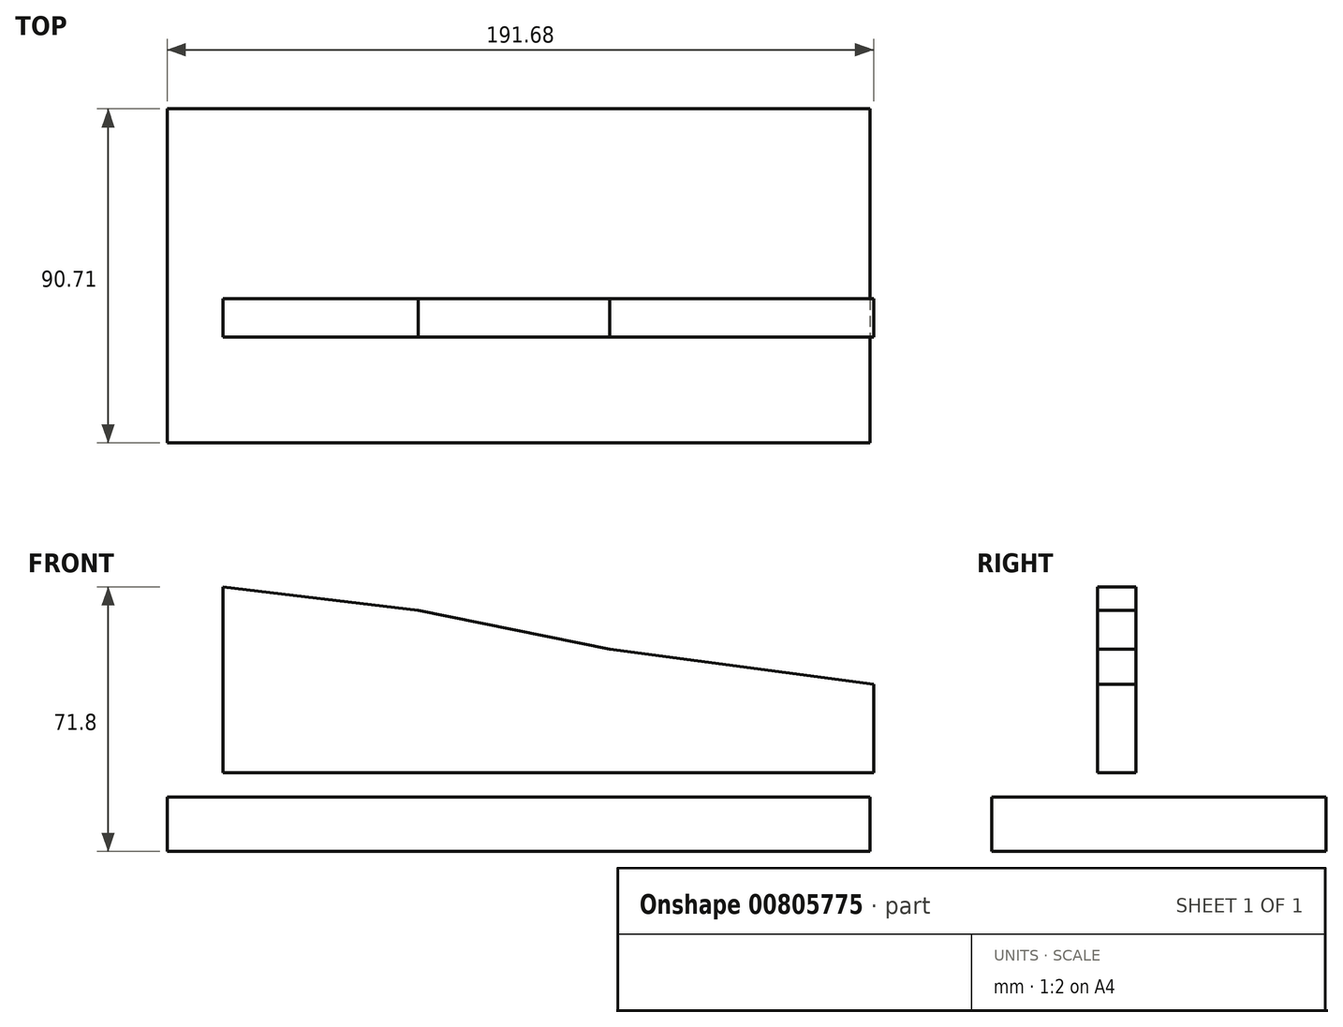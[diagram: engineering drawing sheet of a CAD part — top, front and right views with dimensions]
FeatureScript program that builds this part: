
annotation { "Feature Type Name" : "Feature", "Feature Type Description" : "" }
export const myFeature = defineFeature(function(context is Context, id is Id, definition is map)
    precondition{}
    {
        {
            var Q0;
            Q0=qCreatedBy(makeId("Top.planeOp"),FACE);
            var sketch = newSketch(context, id + "F0", { "sketchPlane" : qUnion([Q0])});
            skLineSegment(sketch, "E0.bottom", {"start": v(-115.05, 51.58) * mm, "end": v(75.7, 51.58) * mm});
            skLineSegment(sketch, "E0.top", {"start": v(-115.05, -39.13) * mm, "end": v(75.7, -39.13) * mm});
            skLineSegment(sketch, "E0.left", {"start": v(-115.05, 51.58) * mm, "end": v(-115.05, -39.13) * mm});
            skLineSegment(sketch, "E0.right", {"start": v(75.7, 51.58) * mm, "end": v(75.7, -39.13) * mm});
            skSolve(sketch);
        }
        {
            var Q0;
            Q0 = qSketchRegion(id + "F0", true);
            extrude(context, id + "F1", {"entities" : qUnion([Q0]), "depth" : 14.73 * mm, "offsetDistance" : 25.4 * mm});
        }
        {
            var Q0;
            Q0=qCreatedBy(makeId("Front.planeOp"),FACE);
            var sketch = newSketch(context, id + "F2", { "sketchPlane" : qUnion([Q0])});
            skLineSegment(sketch, "E1", {"start": v(-99.82, 21.34) * mm, "end": v(76.63, 21.34) * mm});
            skLineSegment(sketch, "E2", {"start": v(76.63, 45.28) * mm, "end": v(76.63, 21.34) * mm});
            skLineSegment(sketch, "E3", {"start": v(76.63, 45.28) * mm, "end": v(5.1, 54.85) * mm});
            skLineSegment(sketch, "E4", {"start": v(-46.91, 65.33) * mm, "end": v(5.1, 54.85) * mm});
            skLineSegment(sketch, "E5", {"start": v(-46.91, 65.33) * mm, "end": v(-99.82, 71.8) * mm});
            skLineSegment(sketch, "E6", {"start": v(-99.82, 71.8) * mm, "end": v(-99.82, 21.34) * mm});
            skSolve(sketch);
        }
        {
            var Q0;
            Q0 = qSketchRegion(id + "F2", true);
            extrude(context, id + "F3", {"entities" : qUnion([Q0]), "depth" : 10.4 * mm, "offsetDistance" : 25.4 * mm});
        }
    });
